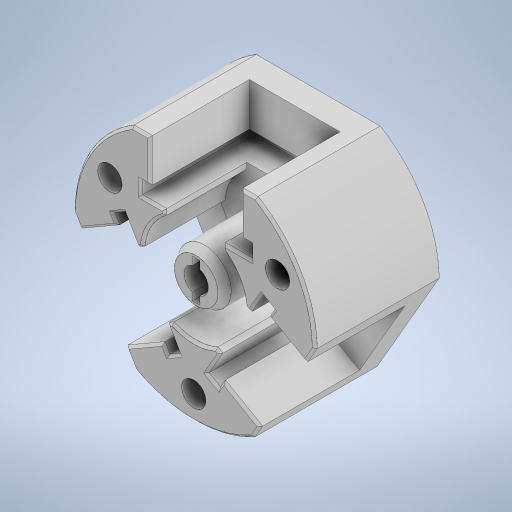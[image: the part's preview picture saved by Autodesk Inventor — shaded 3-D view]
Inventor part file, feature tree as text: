
AUTODESK INVENTOR PART (.ipt)
format: ipt  version: 2023 (Build 270158000, 158)  size: 465,408 bytes
history: native  units: in
note: dims shown in document units (in); Inventor stores cm internally (conversion verified against a paired STEP export)
features: extrude x9, sketch x9, plane x2, pattern_circular x1, other x1
ambient origin geometry x8: Origin, YZ Plane, XZ Plane, XY Plane, X Axis, Y Axis, Z Axis, Center Point
bodies: Solid1 (feature_tree)
feature tree (22):
  extrude  "Extrusion1"  Depth=0.1969in
  extrude  "Extrusion2"  Depth=0.7874in TaperAngle=0.0deg
  pattern_circular  "Circular Pattern1"  Count=3  [1 undecoded]
  extrude  "Extrusion6"  Depth=0.3937in TaperAngle=0.0deg
  extrude  "Extrusion7"  Depth=0.3937in TaperAngle=0.0deg
  extrude  "Extrusion8"  Depth=0.315in
  extrude  "Extrusion9"  Depth=0.3937in TaperAngle=0.0deg
  plane  "Work Plane1"
  extrude  "Extrusion10"  Depth=0.3937in
  extrude  "Extrusion11"  TaperAngle=0.0deg  [1 undecoded]
  plane  "Work Plane2"
  extrude  "Extrusion12"  [1 undecoded]
  sketch  "Sketch2"  dims[d0=0.3937in d1=0.0in d2=0.1969in]
  sketch  "Sketch3"  dims[d3=0.7874in d7=1.1811in d9=0.0in]
  sketch  "Sketch8"  dims[d11=0.0in d12=0.0in d13=1.1811in d14=2.4737in]
  sketch  "Sketch9"  dims[d25=0.3937in d26=0.0in d27=0.3937in d28=0.0in]
  sketch  "Sketch10"  dims[d29=0.1969in d30=0.3937in d31=0.0in]
  sketch  "Sketch11"  dims[d32=0.0591in d33=0.315in]
  sketch  "Sketch13"  dims[d34=0.3937in d35=0.0in d36=0.3937in d37=0.0in]
  sketch  "Sketch14"  dims[d38=0.3937in d39=0.0in d40=0.1181in]
  sketch  "Sketch15"  dims[d41=0.1181in d42=0.0in d43=0.0in]
  other  "Kreismuster2"
note: 3 required parameter values undecoded (feature->parameter linkage not recoverable at this tier; creation-order binding heuristic only, values carry confidence <= 0.55)
